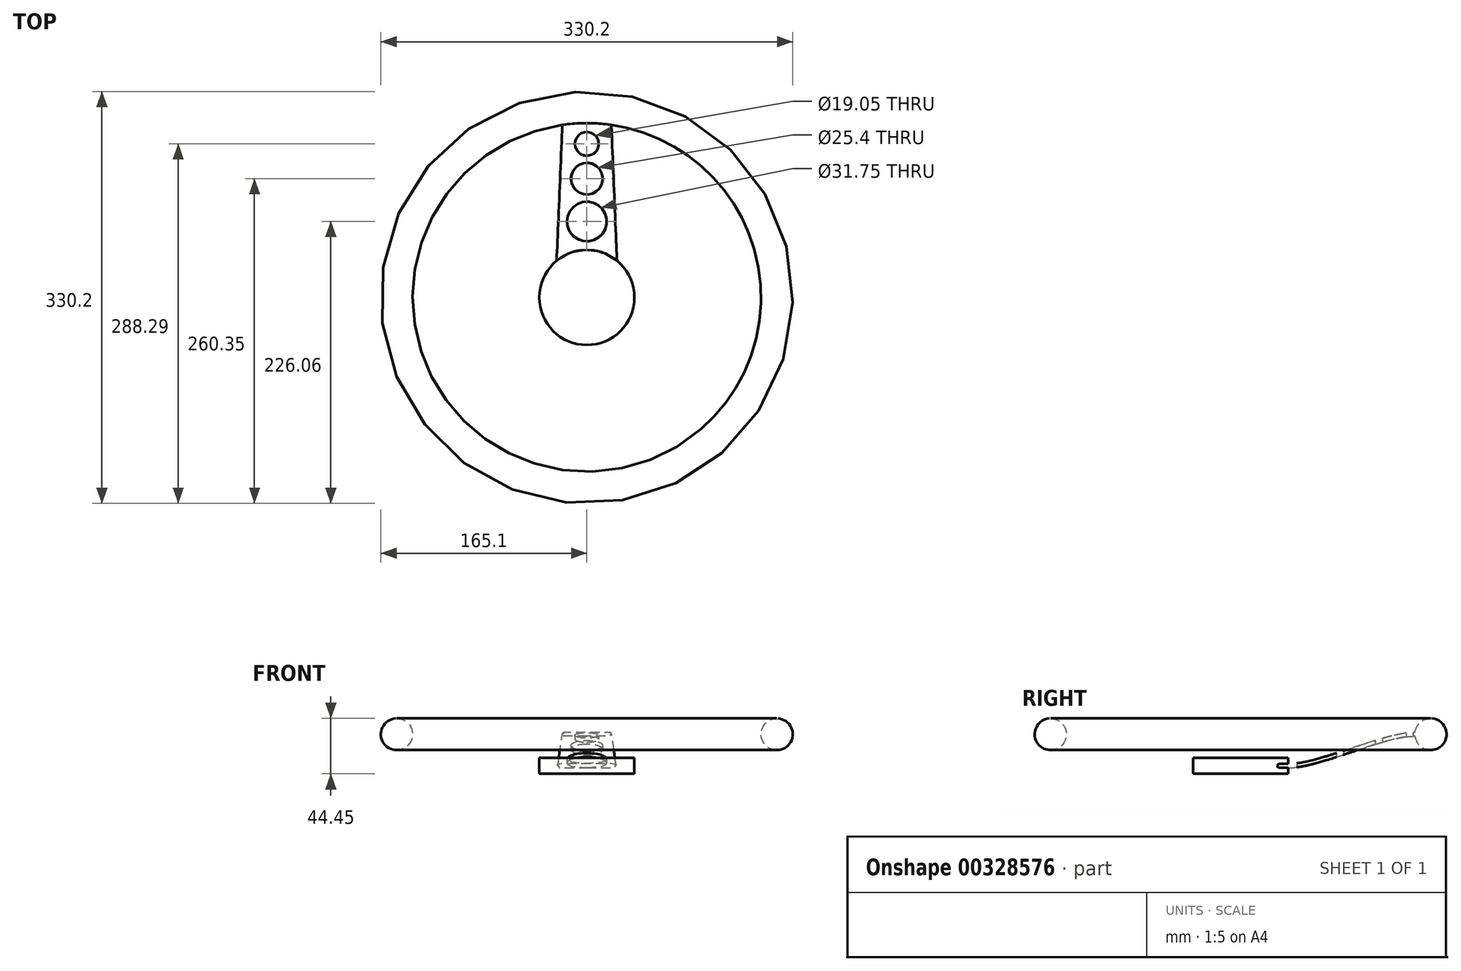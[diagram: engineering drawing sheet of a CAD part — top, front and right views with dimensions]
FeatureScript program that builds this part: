
annotation { "Feature Type Name" : "Feature", "Feature Type Description" : "" }
export const myFeature = defineFeature(function(context is Context, id is Id, definition is map)
    precondition{}
    {
        {
            var Q0;
            Q0=qCreatedBy(makeId("Top.planeOp"),FACE);
            var sketch = newSketch(context, id + "F0", { "sketchPlane" : qUnion([Q0])});
            skCircle(sketch, "E0", {"center": v(0, 0) * mm, "radius": 38.1 * mm});
            skSolve(sketch);
        }
        {
            var Q0;
            Q0=makeQuery(id+"F0.imprint","IMPRINT",FACE,{"disambiguationData":[TD([[makeQuery(id+"F0.imprint","IMPRINT",EDGE,{"derivedFrom":sQuery(id+"F0.wireOp",EDGE,"E0")}),1.0]])]});
            extrude(context, id + "F1", {"entities" : qUnion([Q0]), "depth" : 12.7 * mm, "symmetric" : true});
        }
        {
            var Q0;
            Q0=qCreatedBy(makeId("Right.planeOp"),FACE);
            var sketch = newSketch(context, id + "F2", { "sketchPlane" : qUnion([Q0])});
            skLineSegment(sketch, "E1", {"start": v(0, 0) * mm, "end": v(152.4, 0) * mm, "construction": true});
            skLineSegment(sketch, "E2", {"start": v(152.4, 0) * mm, "end": v(152.4, 25.4) * mm, "construction": true});
            skCircle(sketch, "E3", {"center": v(152.4, 25.4) * mm, "radius": 12.7 * mm});
            skLineSegment(sketch, "E4", {"start": v(0, 0) * mm, "end": v(0, 34.54) * mm, "construction": true});
            skSolve(sketch);
        }
        {
            var Q0;
            Q0=qCreatedBy(makeId("Front.planeOp"),FACE);
            var Q1;
            Q1=sQuery(id+"F2.wireOp",VERTEX,"E3.center");
            cPlane(context, id + "F3", {"entities" : qUnion([Q0, Q1]), "cplaneType" : CPlaneType.PLANE_POINT, "offset" : 25.4 * mm, "width" : 152.4 * mm, "height" : 152.4 * mm});
        }
        {
            var Q0;
            Q0=qCreatedBy(id+"F3.planeOp",FACE);
            var sketch = newSketch(context, id + "F4", { "sketchPlane" : qUnion([Q0])});
            skLineSegment(sketch, "E5.bottom", {"start": v(-17.46, 23.81) * mm, "end": v(17.46, 23.81) * mm});
            skLineSegment(sketch, "E5.top", {"start": v(-17.46, 26.99) * mm, "end": v(17.46, 26.99) * mm});
            skLineSegment(sketch, "E5.left", {"start": v(-19.05, 25.4) * mm, "end": v(-19.05, 25.4) * mm});
            skLineSegment(sketch, "E5.right", {"start": v(19.05, 25.4) * mm, "end": v(19.05, 25.4) * mm});
            skPoint(sketch, "E5.middle", {"position": v(0, 25.4) * mm});
            skPoint(sketch, "E6.visualSharp", {"position": v(-19.05, 26.99) * mm});
            skArc(sketch, "E6.filletArc", {"start": v(-17.46, 26.99) * mm, "mid": v(-18.59, 26.52) * mm, "end": v(-19.05, 25.4) * mm});
            skPoint(sketch, "E7.visualSharp", {"position": v(-19.05, 23.81) * mm});
            skArc(sketch, "E7.filletArc", {"start": v(-19.05, 25.4) * mm, "mid": v(-18.59, 24.28) * mm, "end": v(-17.46, 23.81) * mm});
            skPoint(sketch, "E8.visualSharp", {"position": v(19.05, 23.81) * mm});
            skArc(sketch, "E8.filletArc", {"start": v(17.46, 23.81) * mm, "mid": v(18.59, 24.28) * mm, "end": v(19.05, 25.4) * mm});
            skPoint(sketch, "E9.visualSharp", {"position": v(19.05, 26.99) * mm});
            skArc(sketch, "E9.filletArc", {"start": v(19.05, 25.4) * mm, "mid": v(18.59, 26.52) * mm, "end": v(17.46, 26.99) * mm});
            skSolve(sketch);
        }
        {
            var Q0;
            Q0=qCreatedBy(makeId("Front.planeOp"),FACE);
            var sketch = newSketch(context, id + "F5", { "sketchPlane" : qUnion([Q0])});
            skLineSegment(sketch, "E10.bottom", {"start": v(-23.81, 1.59) * mm, "end": v(23.81, 1.59) * mm});
            skLineSegment(sketch, "E10.top", {"start": v(-23.81, -1.59) * mm, "end": v(23.81, -1.59) * mm});
            skLineSegment(sketch, "E10.left", {"start": v(-25.4, 0) * mm, "end": v(-25.4, 0) * mm});
            skLineSegment(sketch, "E10.right", {"start": v(25.4, 0) * mm, "end": v(25.4, 0) * mm});
            skPoint(sketch, "E10.middle", {"position": v(0, 0) * mm});
            skPoint(sketch, "E11.visualSharp", {"position": v(-25.4, 1.59) * mm});
            skArc(sketch, "E11.filletArc", {"start": v(-23.81, 1.59) * mm, "mid": v(-24.94, 1.12) * mm, "end": v(-25.4, 0) * mm});
            skPoint(sketch, "E12.visualSharp", {"position": v(-25.4, -1.59) * mm});
            skArc(sketch, "E12.filletArc", {"start": v(-25.4, 0) * mm, "mid": v(-24.94, -1.12) * mm, "end": v(-23.81, -1.59) * mm});
            skPoint(sketch, "E13.visualSharp", {"position": v(25.4, -1.59) * mm});
            skArc(sketch, "E13.filletArc", {"start": v(23.81, -1.59) * mm, "mid": v(24.94, -1.12) * mm, "end": v(25.4, 0) * mm});
            skPoint(sketch, "E14.visualSharp", {"position": v(25.4, 1.59) * mm});
            skArc(sketch, "E14.filletArc", {"start": v(25.4, 0) * mm, "mid": v(24.94, 1.12) * mm, "end": v(23.81, 1.59) * mm});
            skSolve(sketch);
        }
        {
            var Q0;
            Q0=qCreatedBy(makeId("Right.planeOp"),FACE);
            var sketch = newSketch(context, id + "F6", { "sketchPlane" : qUnion([Q0])});
            skLineSegment(sketch, "E15", {"start": v(0, -1.59) * mm, "end": v(38.1, -1.59) * mm});
            skLineSegment(sketch, "E16", {"start": v(152.4, 23.81) * mm, "end": v(139.7, 23.81) * mm});
            skLineSegment(sketch, "E17", {"start": v(38.1, 6.35) * mm, "end": v(38.1, -6.35) * mm, "construction": true});
            skFitSpline(sketch, "E18", {"points": [v(38.1, -1.59) * mm, v(139.7, 23.81) * mm], "startDerivative": vector(76.2, 0) * mm, "endDerivative": vector(76.2, 0) * mm});
            skSolve(sketch);
        }
        {
            var Q0;
            Q0=makeQuery(id+"F2.imprint","IMPRINT",FACE,{"disambiguationData":[TD([[makeQuery(id+"F2.imprint","IMPRINT",EDGE,{"derivedFrom":sQuery(id+"F2.wireOp",EDGE,"E3")}),1.0]])]});
            var Q1;
            Q1=sQuery(id+"F2.wireOp",EDGE,"E4");
            revolve(context, id + "F7", {"operationType" : NewBodyOperationType.ADD, "entities" : qUnion([Q0]), "axis" : qUnion([Q1]), "revolveType" : RevolveType.FULL});
        }
        {
            var Q1;
            Q1 = qSketchRegion(id + "F5", true);
            var Q2;
            Q2 = qSketchRegion(id + "F4", true);
            var Q3;
            Q3 = qConstructionFilter(qBodyType(qCreatedBy(id + "F6" ,EDGE), BodyType.WIRE), ConstructionObject.NO);
            loft(context, id + "F8", {"operationType" : NewBodyOperationType.ADD, "addGuides" : true, "sheetProfilesArray" : [{ "sheetProfileEntities" : qUnion([Q1]) }, { "sheetProfileEntities" : qUnion([Q2]) }], "guidesArray" : [{ "guideEntities" : qUnion([Q3]), "guideDerivativeType" : LoftGuideDerivativeType.DEFAULT, "guideDerivativeMagnitude" : 1 }]});
        }
        {
            var Q0;
            Q0=qCreatedBy(makeId("Top.planeOp"),FACE);
            var sketch = newSketch(context, id + "F9", { "sketchPlane" : qUnion([Q0])});
            skCircle(sketch, "E19", {"center": v(0, 60.96) * mm, "radius": 15.88 * mm});
            skCircle(sketch, "E20", {"center": v(0, 95.25) * mm, "radius": 12.7 * mm});
            skCircle(sketch, "E21", {"center": v(0, 123.2) * mm, "radius": 9.53 * mm});
            skSolve(sketch);
        }
        {
            var Q0;
            Q0 = qSketchRegion(id + "F9", true);
            extrude(context, id + "F10", {"entities" : qUnion([Q0]), "operationType" : NewBodyOperationType.REMOVE, "endBound" : BoundingType.THROUGH_ALL, "depth" : 25.4 * mm, "hasSecondDirection" : true, "secondDirectionBound" : BoundingType.THROUGH_ALL, "secondDirectionOppositeDirection" : true, "secondDirectionDepth" : 25.4 * mm});
        }
    });
